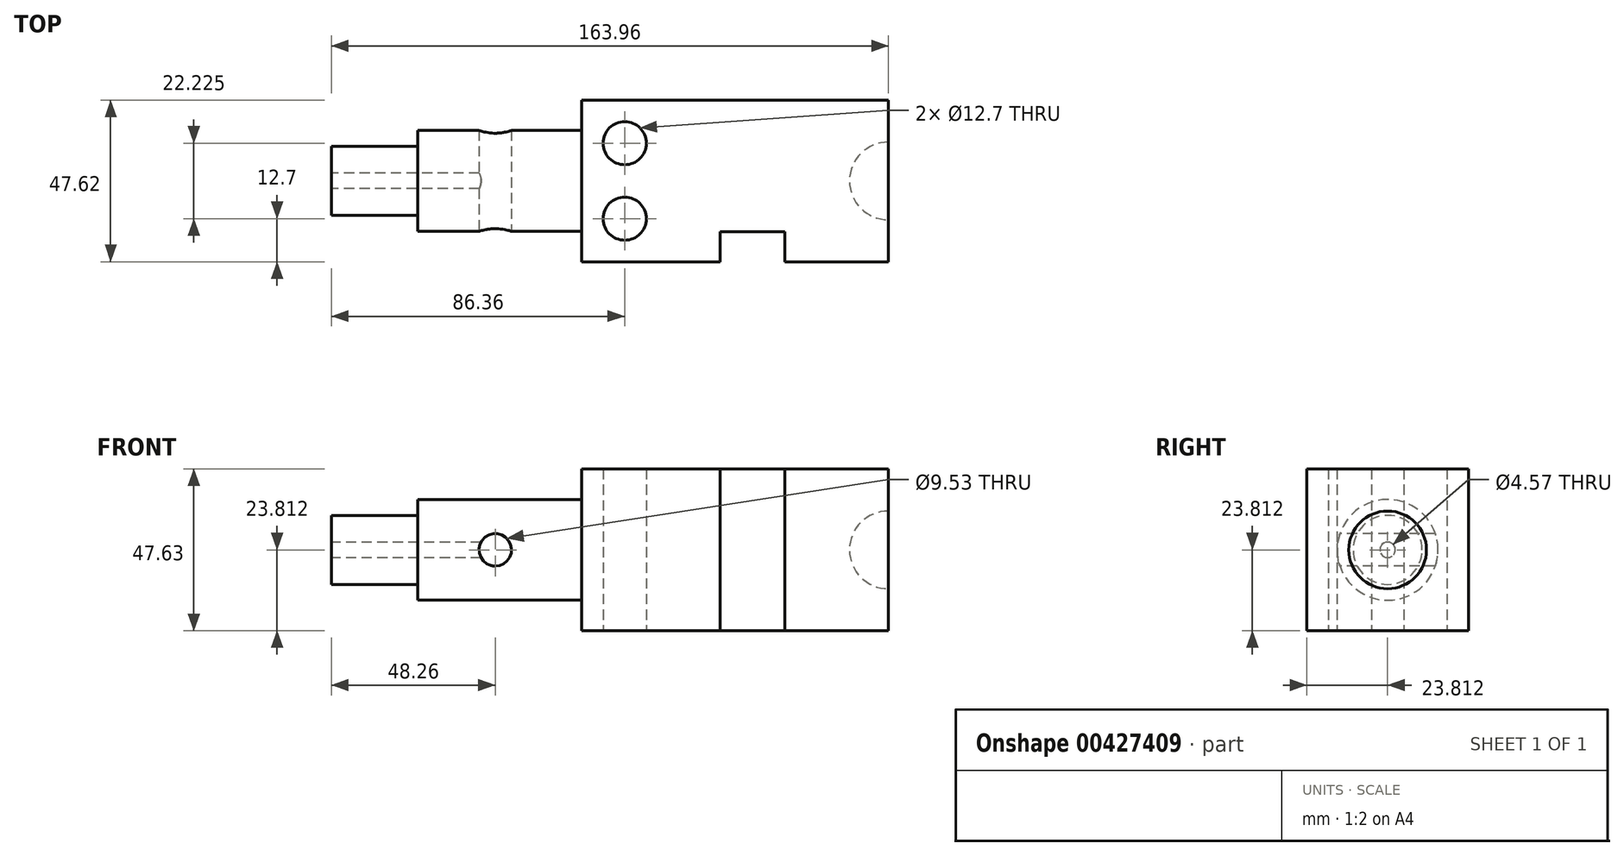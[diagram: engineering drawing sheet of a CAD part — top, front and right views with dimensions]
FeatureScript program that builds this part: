
annotation { "Feature Type Name" : "Feature", "Feature Type Description" : "" }
export const myFeature = defineFeature(function(context is Context, id is Id, definition is map)
    precondition{}
    {
        {
            var Q0;
            Q0=qCreatedBy(makeId("Top.planeOp"),FACE);
            var sketch = newSketch(context, id + "F0", { "sketchPlane" : qUnion([Q0])});
            skLineSegment(sketch, "E0.bottom", {"start": v(0, 0) * mm, "end": v(40.77, 0) * mm});
            skLineSegment(sketch, "E0.top", {"start": v(0, 47.62) * mm, "end": v(90.3, 47.63) * mm});
            skLineSegment(sketch, "E0.left", {"start": v(0, 0) * mm, "end": v(0, 47.62) * mm});
            skLineSegment(sketch, "E0.right", {"start": v(90.3, 0) * mm, "end": v(90.3, 47.63) * mm});
            skLineSegment(sketch, "E1.top", {"start": v(59.82, 8.9) * mm, "end": v(40.77, 8.89) * mm});
            skLineSegment(sketch, "E1.left", {"start": v(59.82, 0) * mm, "end": v(59.82, 8.9) * mm});
            skLineSegment(sketch, "E1.right", {"start": v(40.77, 0) * mm, "end": v(40.77, 8.89) * mm});
            skLineSegment(sketch, "E2.trimOffspring", {"start": v(59.82, 0) * mm, "end": v(90.3, 0) * mm});
            skCircle(sketch, "E3", {"center": v(12.7, 12.7) * mm, "radius": 6.35 * mm});
            skCircle(sketch, "E4", {"center": v(12.7, 34.92) * mm, "radius": 6.35 * mm});
            skSolve(sketch);
        }
        {
            var Q0;
            Q0 = qSketchRegion(id + "F0", true);
            extrude(context, id + "F1", {"entities" : qUnion([Q0]), "depth" : 47.62 * mm});
        }
        {
            var Q0;
            Q0=makeQuery(id+"F1.opExtrude","CAP_FACE",FACE,{"disambiguationData":[OSD([sQuery(id+"F0.wireOp",EDGE,"E0.bottom"),sQuery(id+"F0.wireOp",EDGE,"E0.top"),sQuery(id+"F0.wireOp",EDGE,"E0.left"),sQuery(id+"F0.wireOp",EDGE,"E0.right"),sQuery(id+"F0.wireOp",EDGE,"E1.top"),sQuery(id+"F0.wireOp",EDGE,"E1.left"),sQuery(id+"F0.wireOp",EDGE,"E1.right"),sQuery(id+"F0.wireOp",EDGE,"E2.trimOffspring"),sQuery(id+"F0.wireOp",EDGE,"E3"),sQuery(id+"F0.wireOp",EDGE,"E4")])],"isStart":true});
            cPlane(context, id + "F2", {"entities" : qUnion([Q0]), "cplaneType" : CPlaneType.OFFSET, "offset" : 23.8 * mm, "oppositeDirection" : true, "width" : 152.4 * mm, "height" : 152.4 * mm});
        }
        {
            var Q0;
            Q0=qCreatedBy(id+"F2.planeOp",FACE);
            var sketch = newSketch(context, id + "F3", { "sketchPlane" : qUnion([Q0])});
            skLineSegment(sketch, "E5.0", {"start": v(90.3, -12.38) * mm, "end": v(90.3, -35.24) * mm});
            skArc(sketch, "E6", {"start": v(90.3, -12.38) * mm, "mid": v(78.87, -23.81) * mm, "end": v(90.3, -35.24) * mm});
            skPoint(sketch, "E7.orphan", {"position": v(90.3, -47.63) * mm});
            skPoint(sketch, "E8.orphan", {"position": v(90.3, 0) * mm});
            skSolve(sketch);
        }
        {
            var Q0;
            Q0 = qSketchRegion(id + "F3", true);
            var Q1;
            Q1=sQuery(id+"F3.wireOp",EDGE,"E5.0");
            revolve(context, id + "F4", {"operationType" : NewBodyOperationType.REMOVE, "entities" : qUnion([Q0]), "axis" : qUnion([Q1]), "revolveType" : RevolveType.FULL, "oppositeDirection" : true});
        }
        {
            var Q0;
            Q0=makeQuery(id+"F1.opExtrude","SWEPT_FACE",FACE,{"disambiguationData":[OSD([sQuery(id+"F0.wireOp",EDGE,"E0.left")])]});
            var sketch = newSketch(context, id + "F5", { "sketchPlane" : qUnion([Q0])});
            skLineSegment(sketch, "E9", {"start": v(-23.81, 47.63) * mm, "end": v(-23.81, 0) * mm, "construction": true});
            skCircle(sketch, "E10", {"center": v(-23.81, 23.81) * mm, "radius": 14.84 * mm});
            skSolve(sketch);
        }
        {
            var Q0;
            Q0=makeQuery(id+"F5.imprint","IMPRINT",FACE,{"disambiguationData":[TD([[makeQuery(id+"F5.imprint","IMPRINT",EDGE,{"derivedFrom":sQuery(id+"F5.wireOp",EDGE,"E10")}),1.0]])]});
            var Q1;
            Q1=sQuery(id+"F5.wireOp",EDGE,"E10");
            extrude(context, id + "F6", {"entities" : qUnion([Q0]), "operationType" : NewBodyOperationType.ADD, "surfaceEntities" : qUnion([Q1]), "depth" : 48.26 * mm});
        }
        {
            var Q0;
            Q0=makeQuery(id+"F6.opExtrude","CAP_FACE",FACE,{"disambiguationData":[OSD([sQuery(id+"F5.wireOp",EDGE,"E10")])],"isStart":false});
            var sketch = newSketch(context, id + "F7", { "sketchPlane" : qUnion([Q0])});
            skCircle(sketch, "E11", {"center": v(-23.81, 23.81) * mm, "radius": 10.16 * mm});
            skSolve(sketch);
        }
        {
            var Q0;
            Q0 = qSketchRegion(id + "F7", true);
            extrude(context, id + "F8", {"entities" : qUnion([Q0]), "operationType" : NewBodyOperationType.ADD, "depth" : 25.4 * mm});
        }
        {
            var Q0;
            Q0=makeQuery(id+"F8.opExtrude","CAP_FACE",FACE,{"disambiguationData":[OSD([sQuery(id+"F7.wireOp",EDGE,"E11")])],"isStart":false});
            var sketch = newSketch(context, id + "F9", { "sketchPlane" : qUnion([Q0])});
            skCircle(sketch, "E12", {"center": v(-23.81, 23.81) * mm, "radius": 2.29 * mm});
            skSolve(sketch);
        }
        {
            var Q0;
            Q0=qCreatedBy(makeId("Front.planeOp"),FACE);
            var sketch = newSketch(context, id + "F10", { "sketchPlane" : qUnion([Q0])});
            skLineSegment(sketch, "E13.0", {"start": v(0, 47.63) * mm, "end": v(0, 0) * mm, "construction": true});
            skLineSegment(sketch, "E14", {"start": v(0, 23.81) * mm, "end": v(-25.4, 23.81) * mm, "construction": true});
            skCircle(sketch, "E15", {"center": v(-25.4, 23.81) * mm, "radius": 4.76 * mm});
            skSolve(sketch);
        }
        {
            var Q0;
            Q0 = qSketchRegion(id + "F10", true);
            extrude(context, id + "F11", {"entities" : qUnion([Q0]), "operationType" : NewBodyOperationType.REMOVE, "oppositeDirection" : true, "depth" : 127 * mm});
        }
        {
            var Q0;
            Q0 = qSketchRegion(id + "F9", true);
            extrude(context, id + "F12", {"entities" : qUnion([Q0]), "operationType" : NewBodyOperationType.REMOVE, "endBound" : BoundingType.UP_TO_NEXT, "oppositeDirection" : true, "depth" : 25.4 * mm});
        }
    });
